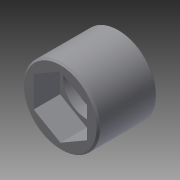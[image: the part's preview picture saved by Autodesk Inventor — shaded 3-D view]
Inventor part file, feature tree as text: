
AUTODESK INVENTOR PART (.ipt)
format: ipt  version: 2014 SP2 (Build 180246200, 246)  size: 122,368 bytes
history: native  units: in
note: dims shown in document units (in); Inventor stores cm internally (conversion verified against a paired STEP export)
features: other x7, sketch x2, revolve x1, thread x1, extrude x1
ambient origin geometry x8: Origin, YZ Plane, XZ Plane, XY Plane, X Axis, Y Axis, Z Axis, Center Point
bodies: Solid1 (feature_tree)
feature tree (12):
  revolve  "Revolution1"  [1 undecoded]
  thread  "Thread1"  [1 undecoded]
  extrude  "Extrusion1"  [1 undecoded]
  other  "screw_XY"
  other  "screw_YZ"
  other  "screw_ZX"
  other  "screw_X"
  other  "screw_Y"
  other  "screw_Z"
  other  "screw_Center"
  sketch  "Sketch_1"  dims[d0=360.0deg d1=0.0622in d2=0.0in d3=0.077in d4=0.0in]
  sketch  "Sketch_3"  dims[d5=0.0in]
note: 3 required parameter values undecoded (feature->parameter linkage not recoverable at this tier; creation-order binding heuristic only, values carry confidence <= 0.55)